# Revit family: Bath spout_TOTO_TBS03001
name_source: partatom
category: 衛生器具
revit_build: Autodesk Revit 2018 (Build: 20170223_1515(x64)
units: mm (PartAtom-declared; Revit-internal decimal feet)

## family parameters
OmniClass タイトル = Sanitary, Laundry, and Cleaning Equipment
OmniClass 番号 = 23.45.00.00
パーツ タイプ = 標準
ロード時にボイドで切り取り = いいえ
丸型コネクタ寸法 = 直径を使用
作業面ベース = いいえ
共有 = いいえ
常に垂直 = はい
部屋計算ポイント = いいえ

## types (1)
- Bath spout_TOTO_TBS03001
    Finish = faucet_material
    Height = 67  [stored 0.219816 ft]
    Length = 169  [stored 0.554462 ft]
    TOTO AsiaOceania = TBS03001B
    TOTO AsiaOceania URL = http://asia.toto.com
    TOTO China = TBS03001B
    TOTO China URL = http://www.toto.com.cn
    TOTO HongKong = TBS03001B
    TOTO HongKong URL = http://hk.toto.com
    TOTO India = TBS03001B
    TOTO India URL = https://in.toto.com
    TOTO Taiwan = TBS03001B
    TOTO Taiwan URL = https://www.twtoto.com.tw
    TOTO Taiwan URL 02 = https://www.twtoto.com.tw
    TOTO Taiwan URL 03 = https://www.twtoto.com.tw
    TOTO Taiwan URL 04 = https://www.twtoto.com.tw
    TOTO Taiwan URL 05 = https://www.twtoto.com.tw
    TOTO Taiwan URL 06 = https://www.twtoto.com.tw
    TOTO Taiwan URL 07 = https://www.twtoto.com.tw
    TOTO Taiwan URL 08 = https://www.twtoto.com.tw
    TOTO Taiwan URL 09 = https://www.twtoto.com.tw
    TOTO Taiwan URL 10 = https://www.twtoto.com.tw
    TOTO Taiwan URL 11 = https://www.twtoto.com.tw
    TOTO Taiwan URL 12 = https://www.twtoto.com.tw
    TOTO Taiwan URL 13 = https://www.twtoto.com.tw
    TOTO Taiwan URL 14 = https://www.twtoto.com.tw
    TOTO Taiwan URL 15 = https://www.twtoto.com.tw
    TOTO Taiwan URL 16 = https://www.twtoto.com.tw
    TOTO Taiwan URL 17 = https://www.twtoto.com.tw
    TOTO Taiwan URL 18 = https://www.twtoto.com.tw
    TOTO Taiwan URL 19 = https://www.twtoto.com.tw
    TOTO Taiwan URL 20 = https://www.twtoto.com.tw
    TOTO Taiwan URL 21 = https://www.twtoto.com.tw
    TOTO Taiwan URL 22 = https://www.twtoto.com.tw
    TOTO Thailand = TBS03001T
    TOTO Thailand URL = https://th.toto.com
    TOTO Vietnam = TBS03001B
    TOTO Vietnam URL = https://vn.toto.com
    Width = 67  [stored 0.219816 ft]
    モデル = TBS03001
    製造元 = TOTO Ltd.
    説明 = Bath spout/吐水口

note: [stored X ft] marks values corroborated as IEEE doubles in the binary element streams (Revit-internal decimal feet)

## geometry (parser evidence)
native form markers: Sweep x2
no freeform markers — native parametric forms only
